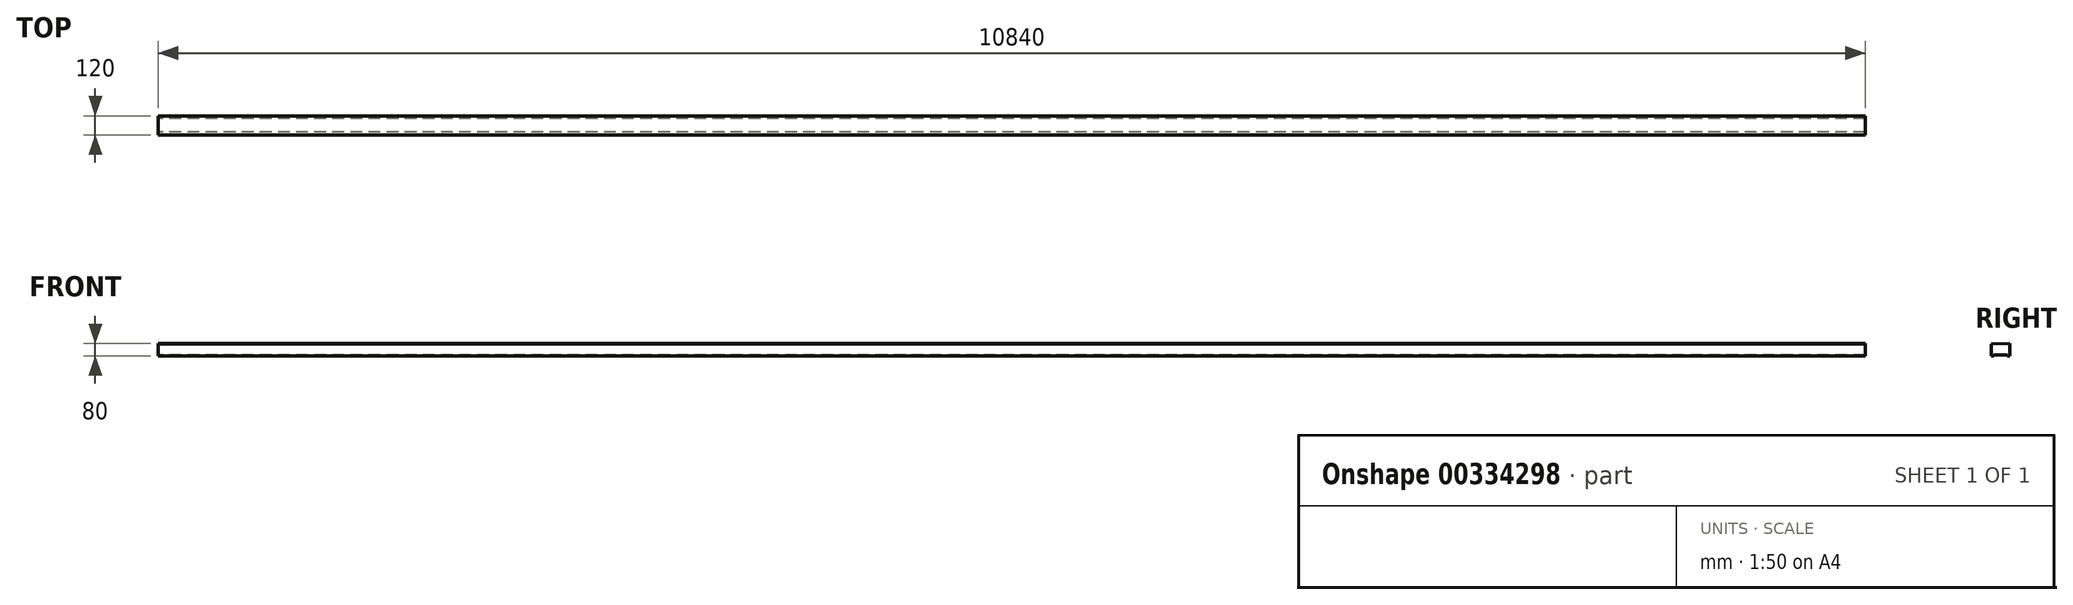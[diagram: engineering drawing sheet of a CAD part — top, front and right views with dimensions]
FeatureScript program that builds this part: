
annotation { "Feature Type Name" : "Feature", "Feature Type Description" : "" }
export const myFeature = defineFeature(function(context is Context, id is Id, definition is map)
    precondition{}
    {
        {
            var Q0;
            Q0=qCreatedBy(makeId("Right.planeOp"),FACE);
            var sketch = newSketch(context, id + "F0", { "sketchPlane" : qUnion([Q0])});
            skLineSegment(sketch, "E0.top", {"start": v(0, 80) * mm, "end": v(-120, 80) * mm, "construction": true});
            skLineSegment(sketch, "E0.left", {"start": v(0, 0) * mm, "end": v(0, 80) * mm});
            skLineSegment(sketch, "E1", {"start": v(-60, 80) * mm, "end": v(-60, 0) * mm, "construction": true});
            skLineSegment(sketch, "E2", {"start": v(0, 0) * mm, "end": v(-18, 0) * mm});
            skLineSegment(sketch, "E3", {"start": v(-18, 0) * mm, "end": v(-18, 8) * mm});
            skLineSegment(sketch, "E4", {"start": v(-18, 8) * mm, "end": v(-102, 8) * mm});
            skLineSegment(sketch, "E5", {"start": v(-102, 8) * mm, "end": v(-102, 0) * mm});
            skLineSegment(sketch, "E6", {"start": v(-102, 0) * mm, "end": v(-120, 0) * mm});
            skPoint(sketch, "E7", {"position": v(-120, 77.6) * mm});
            skLineSegment(sketch, "E8", {"start": v(0, 80) * mm, "end": v(-120, 77.6) * mm});
            skLineSegment(sketch, "E9", {"start": v(-120, 77.6) * mm, "end": v(-120, 0) * mm});
            skLineSegment(sketch, "E10", {"start": v(-120, 80) * mm, "end": v(-120, 77.6) * mm, "construction": true});
            skSolve(sketch);
        }
        {
            var Q0;
            Q0=makeQuery(id+"F0.imprint","IMPRINT",FACE,{"disambiguationData":[TD([[makeQuery(id+"F0.imprint","IMPRINT",EDGE,{"derivedFrom":sQuery(id+"F0.wireOp",EDGE,"E0.top")}),1.0]])]});
            var Q1;
            Q1=makeQuery(id+"F0.imprint","IMPRINT",FACE,{"disambiguationData":[TD([[makeQuery(id+"F0.imprint","IMPRINT",EDGE,{"derivedFrom":sQuery(id+"F0.wireOp",EDGE,"E0.left")}),1.0]])]});
            extrude(context, id + "F1", {"entities" : qUnion([Q0, Q1]), "depth" : 10840 * mm});
        }
    });
